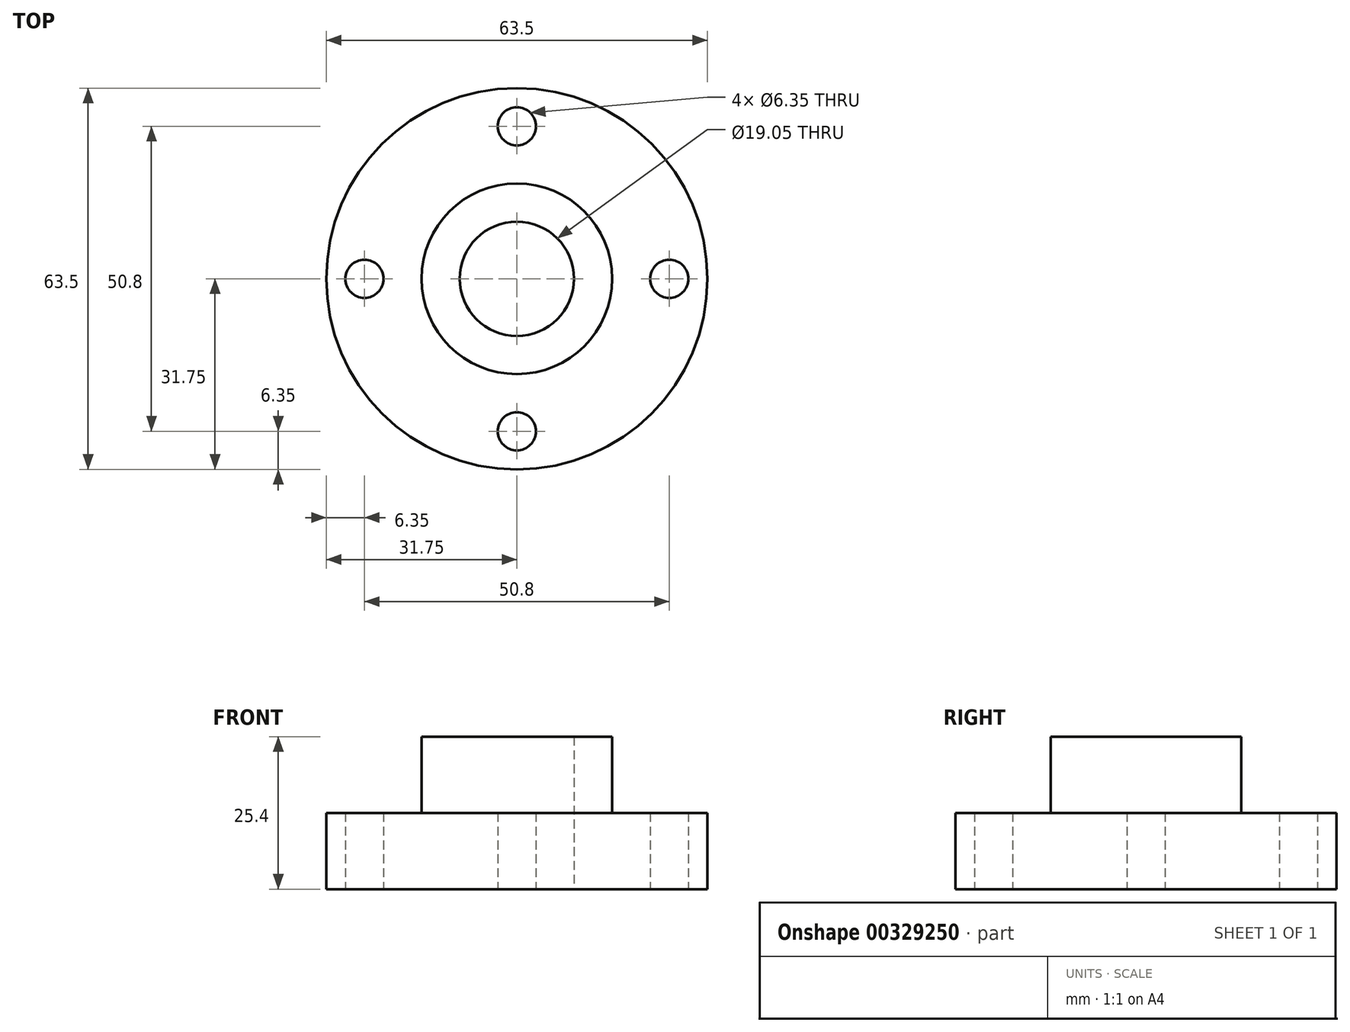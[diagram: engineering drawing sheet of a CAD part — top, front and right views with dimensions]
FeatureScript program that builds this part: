
annotation { "Feature Type Name" : "Feature", "Feature Type Description" : "" }
export const myFeature = defineFeature(function(context is Context, id is Id, definition is map)
    precondition{}
    {
        {
            var Q0;
            Q0=qCreatedBy(makeId("Top.planeOp"),FACE);
            var sketch = newSketch(context, id + "F0", { "sketchPlane" : qUnion([Q0])});
            skCircle(sketch, "E0", {"center": v(0, 0) * mm, "radius": 31.75 * mm});
            skCircle(sketch, "E1", {"center": v(0, 0) * mm, "radius": 9.53 * mm});
            skCircle(sketch, "E2", {"center": v(0, 25.4) * mm, "radius": 3.18 * mm});
            skCircle(sketch, "E3", {"center": v(25.4, 0) * mm, "radius": 3.18 * mm});
            skCircle(sketch, "E4", {"center": v(-25.4, 0) * mm, "radius": 3.18 * mm});
            skCircle(sketch, "E5", {"center": v(0, -25.4) * mm, "radius": 3.18 * mm});
            skCircle(sketch, "E6", {"center": v(0, 0) * mm, "radius": 25.4 * mm, "construction": true});
            skSolve(sketch);
        }
        {
            var Q0;
            Q0 = qSketchRegion(id + "F0", true);
            extrude(context, id + "F1", {"entities" : qUnion([Q0]), "depth" : 12.7 * mm});
        }
        {
            var Q0;
            Q0=qCreatedBy(makeId("Top.planeOp"),FACE);
            var sketch = newSketch(context, id + "F2", { "sketchPlane" : qUnion([Q0])});
            skCircle(sketch, "E7", {"center": v(0, 0) * mm, "radius": 15.88 * mm});
            skCircle(sketch, "E8", {"center": v(0, 0) * mm, "radius": 9.53 * mm});
            skSolve(sketch);
        }
        {
            var Q0;
            Q0 = qSketchRegion(id + "F2", true);
            extrude(context, id + "F3", {"entities" : qUnion([Q0]), "operationType" : NewBodyOperationType.ADD, "depth" : 25.4 * mm});
        }
    });
